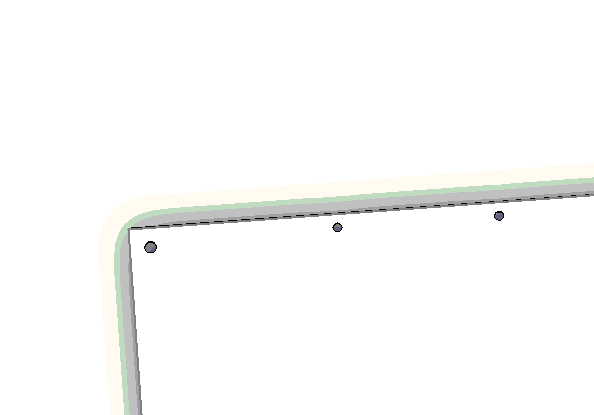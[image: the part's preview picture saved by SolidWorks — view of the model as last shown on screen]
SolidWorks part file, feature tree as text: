
SOLIDWORKS PART (.sldprt)
format: sldprt  version: not decoded by parser v0  size: 286,720 bytes
history: native  units: mm
features: sketch x6, cut_extrude x5, extrude x1, pattern_linear x1 (+11 scaffold rows collapsed)
feature tree (24):
  scaffold x11  (default folders/planes/origin — collapsed)
  sketch  "Sketch1"  dims[D1=100.6602mm D2=190.5mm]
  extrude  "Extrude1"  Depth=1.6002mm
  sketch  "Sketch2"  dims[c1.D1=3.556mm c1.D2=3.556mm c1.D3=3.556mm c1.D4=3.556mm c1.D5=6.35mm c1.D6=6.35mm c1.D7=6.35mm c1.D8=6.35mm c1.D9=6.35mm c2.D1=6.35mm]
  cut_extrude  "Cut-Extrude1"  Depth=1.6002mm
  sketch  "Sketch3"  dims[D1=2.794mm D2=2.794mm D3=4.445mm D4=49.3268mm D5=63.5mm]
  cut_extrude  "Cut-Extrude2"  Depth=10mm
  pattern_linear  "LPattern1"  Count1=2 Count2=2 Spacing1=84.7852mm Spacing2=177.8mm
  sketch  "Sketch4"  dims[c1.D1=1.016mm c1.D2=1.016mm c1.D5=1.016mm c1.D6=1.016mm c1.D3=7.62mm c1.D4=3.048mm c1.D7=7.62mm c1.D8=2.54mm c1.D9=76.2mm c2.D7=7.62mm c2.D3=17.78mm c2.D4=3.048mm]
  cut_extrude  "Cut-Extrude3"  Depth=7.62mm
  sketch  "Sketch5"  dims[D1=2.3mm D2=2.3mm D6=1.2mm D7=1.2mm D3=41.37mm D4=22.86mm D5=20.32mm D8=44.07mm D9=2.4mm D10=1.35mm]
  cut_extrude  "Cut-Extrude4"  Depth=2.54mm
  sketch  "Sketch6"  dims[D1=2.3114mm D2=2.3114mm D3=12.0396mm D4=7.62mm D5=~73.181324mm]
  cut_extrude  "Cut-Extrude5"  Depth=2.54mm
decode coverage: 13 of 13 modeling features carry decoded parameters
note: ~ marks probable driven/reference dimensions
note: suppression state not decoded; provenance and decode notes live in map.json
